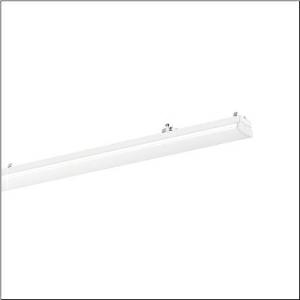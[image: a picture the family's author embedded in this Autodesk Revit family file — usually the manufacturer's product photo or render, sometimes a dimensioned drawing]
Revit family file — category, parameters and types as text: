
# Revit family: licross_r__11_recessed_opal_mo_51tl1d7n44xg_4ee8
name_source: partatom
category: Lighting Fixtures
units: mm (PartAtom-declared; Revit-internal decimal feet)

## family parameters
Cut with Voids When Loaded = No
Host = Face
Light Source = No
Part Type = Normal
Room Calculation Point = No
Round Connector Dimension = Use Diameter
Shared = No

## types (1)
- Licross® 11 recessed opal MO (1 x LED, 4480 lm, 24.8 W, 4000K)
    Apparent Load = 25 VA
    CIE Flux Codes = 44 73 91 87 100
    Color Rendering = 80
    Color Temperature = 4000K
    Default Elevation = 1800 mm
    Description = Licross® 11 recessed opal MO, luminaire insert, of sheet steel, coil coated, white, length: 1.500mm, width: 76mm, height: 87mm, LED rated luminous flux: 4.480lm, light colour: 840, control gear: ON/OFF, with plug, 3-pole, with phase selection, mains connection: 220..240V, AC, 50/60Hz, rated input power: 25W, halogen-free wiring, primary optical cover: cover, of PMMA, light emission: direct with ceiling illumination distribution, primary light characteristic: symmetric, protection rating (complete): IP40, insulation class (complete): insulation class I (protective earthing), certification: CE, ENEC, VDE, UKCA, protection symbol: D if used in an environment without relevant dust loads with corresponding accessories, impact resistance: IK06, permissible ambient temperature for indoor applications: -35..+45°C, corresponds to IFS (International Featured Standards) requirements for safety and quality in the food industry, reducing of maximum allowable ambient temperature of 5°C with ceiling mounting, packaging unit: 1 piece
    Height = 83 mm
    Lamp = 1 x LED
    Lamp Light Flux = 4480 lm
    Lamp Power = 24.8 W
    Lamp count = 1
    Length = 1500 mm
    Luminous efficacy = 181 lm/W
    Manufacturer = Siteco
    ModVariant = No
    Model = 51TL1D7N44XG
    Mounting Place = Ceiling
    Mounting Type = Pendant
    Number of Poles = 1
    OnlyDefault = Yes
    Power Factor = 1
    Product Name = Licross® 11 recessed opal MO
    Product group = luminaire insert
    ProductGroupID = 902
    Protection Class = Protection class I
    Protection Degree = IP 40
    RLX_Detail_Level = 1
    RLX_Emergency_Light_Flux = 0 lm
    RLX_Emergency_Type = 0
    RLX_Emergency_Type_DB = No
    RlxData = <blob elided: 23045 chars, md5=d6b7e539>
    Socket = socket
    Standby Power = 0 W
    System Light Flux = 4480 lm
    System Power = 25 W
    Type Comments = Product without accessories
    Type Image = l_1313666.jpg
    URL = http://relux.com
    VarID = ---
    Voltage = 0 V
    Weight = 0.00 kg
    Width = 76 mm

## geometry (parser evidence)
native form markers: Blend x4, Sweep x13
no freeform markers — native parametric forms only
